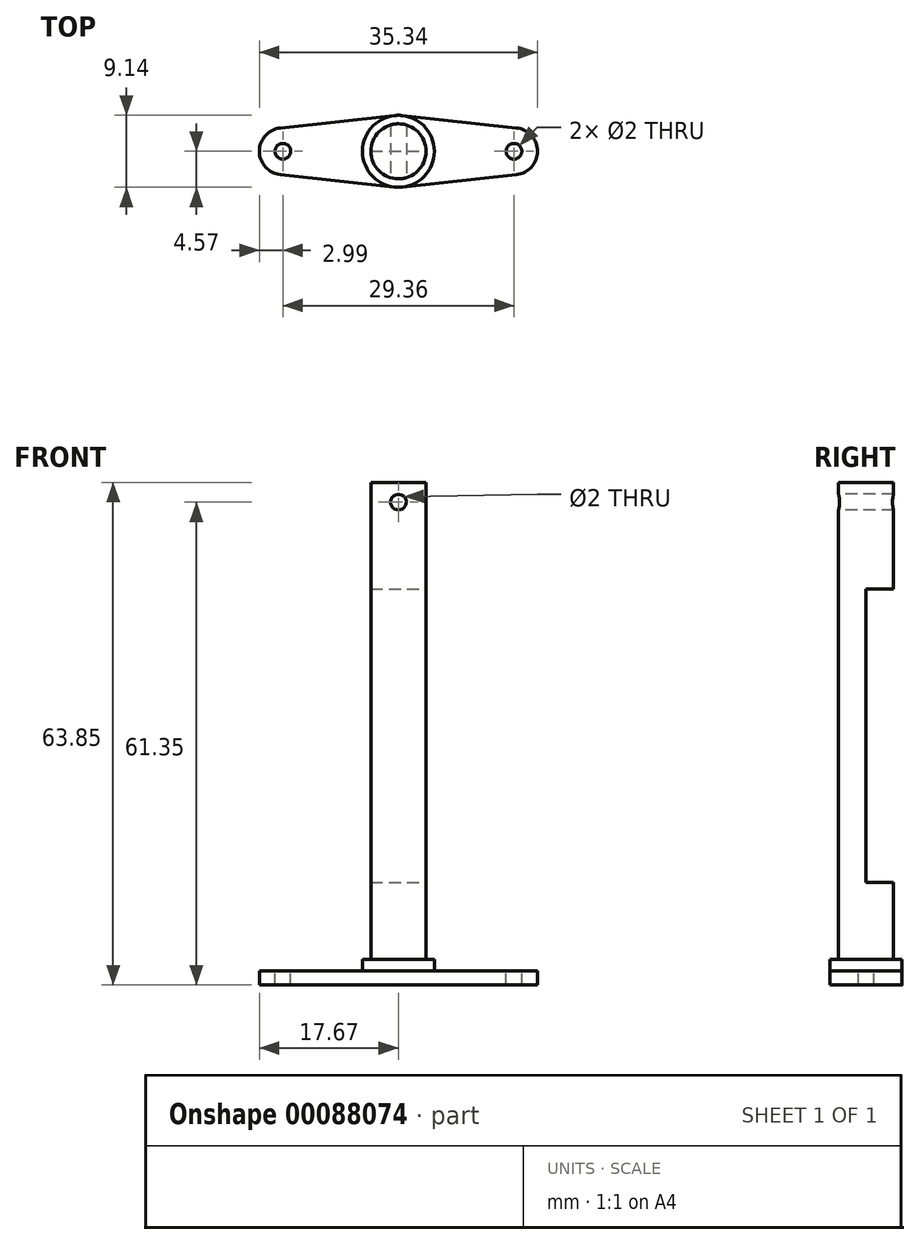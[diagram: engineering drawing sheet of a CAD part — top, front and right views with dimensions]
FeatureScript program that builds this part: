
annotation { "Feature Type Name" : "Feature", "Feature Type Description" : "" }
export const myFeature = defineFeature(function(context is Context, id is Id, definition is map)
    precondition{}
    {
        {
            var Q0;
            Q0=qCreatedBy(makeId("Top.planeOp"),FACE);
            var sketch = newSketch(context, id + "F0", { "sketchPlane" : qUnion([Q0])});
            skCircle(sketch, "E0", {"center": v(0, 0) * mm, "radius": 3.5 * mm});
            skSolve(sketch);
        }
        {
            var Q0;
            Q0 = qSketchRegion(id + "F0", true);
            extrude(context, id + "F1", {"entities" : qUnion([Q0]), "depth" : 56.35 * mm, "hasSecondDirection" : true, "secondDirectionOppositeDirection" : true, "secondDirectionDepth" : 1.5 * mm});
        }
        {
            var Q0;
            Q0=qCreatedBy(makeId("Top.planeOp"),FACE);
            var sketch = newSketch(context, id + "F2", { "sketchPlane" : qUnion([Q0])});
            skCircle(sketch, "E1", {"center": v(-14.68, 0) * mm, "radius": 1 * mm});
            skCircle(sketch, "E2.MirrorC", {"center": v(14.68, 0) * mm, "radius": 1 * mm});
            skArc(sketch, "E3", {"start": v(-15, 2.97) * mm, "mid": v(-16.9, 2) * mm, "end": v(-17.67, 0) * mm});
            skLineSegment(sketch, "E4", {"start": v(0, 0) * mm, "end": v(0, 4.6) * mm, "construction": true});
            skLineSegment(sketch, "E5", {"start": v(-15, 2.97) * mm, "end": v(0, 4.6) * mm});
            skLineSegment(sketch, "E6.MirrorCS", {"start": v(-15, -2.97) * mm, "end": v(0, -4.6) * mm});
            skArc(sketch, "E7.MirrorCS", {"start": v(-15, -2.97) * mm, "mid": v(-16.9, -2) * mm, "end": v(-17.67, 0) * mm});
            skLineSegment(sketch, "E8.MirrorCS", {"start": v(15, 2.97) * mm, "end": v(0, 4.6) * mm});
            skArc(sketch, "E9.MirrorCS", {"start": v(15, 2.97) * mm, "mid": v(16.9, 2) * mm, "end": v(17.67, 0) * mm});
            skArc(sketch, "E10.MirrorCS", {"start": v(15, -2.97) * mm, "mid": v(16.9, -2) * mm, "end": v(17.67, 0) * mm});
            skLineSegment(sketch, "E11.MirrorCS", {"start": v(15, -2.97) * mm, "end": v(0, -4.6) * mm});
            skSolve(sketch);
        }
        {
            var Q0;
            Q0 = qSketchRegion(id + "F2", true);
            extrude(context, id + "F3", {"entities" : qUnion([Q0]), "operationType" : NewBodyOperationType.ADD, "oppositeDirection" : true, "depth" : 2 * mm});
        }
        {
            var Q0;
            Q0=makeQuery(id+"F3.opExtrude","SWEPT_EDGE",EDGE,{"disambiguationData":[OSD([sQuery(id+"F2.wireOp",EDGE,"E5"),sQuery(id+"F2.wireOp",EDGE,"E8.MirrorCS")])]});
            fillet(context, id + "F4", {"entities" : qUnion([Q0]), "radius" : 5 * mm, "tangentPropagation" : true, "allowEdgeOverflow" : false});
        }
        {
            var Q0;
            Q0=makeQuery(id+"F3.opExtrude","SWEPT_EDGE",EDGE,{"disambiguationData":[OSD([sQuery(id+"F2.wireOp",EDGE,"E6.MirrorCS"),sQuery(id+"F2.wireOp",EDGE,"E11.MirrorCS")])]});
            fillet(context, id + "F5", {"entities" : qUnion([Q0]), "radius" : 5 * mm, "tangentPropagation" : true, "allowEdgeOverflow" : false});
        }
        {
            var Q0;
            Q0=qCreatedBy(makeId("Front.planeOp"),FACE);
            var sketch = newSketch(context, id + "F6", { "sketchPlane" : qUnion([Q0])});
            skLineSegment(sketch, "E12", {"start": v(4.63, 9.53) * mm, "end": v(4.63, 28.18) * mm});
            skLineSegment(sketch, "E13", {"start": v(4.63, 28.18) * mm, "end": v(-5.26, 28.18) * mm});
            skLineSegment(sketch, "E14", {"start": v(-5.26, 28.18) * mm, "end": v(-5.26, 9.53) * mm});
            skLineSegment(sketch, "E15", {"start": v(-19.44, 28.18) * mm, "end": v(29.53, 28.18) * mm, "construction": true});
            skLineSegment(sketch, "E16", {"start": v(-5.26, 9.53) * mm, "end": v(4.63, 9.53) * mm});
            skLineSegment(sketch, "E17.MirrorCS", {"start": v(-5.26, 28.18) * mm, "end": v(-5.26, 46.83) * mm});
            skLineSegment(sketch, "E18.MirrorCS", {"start": v(-5.26, 46.83) * mm, "end": v(4.63, 46.83) * mm});
            skLineSegment(sketch, "E19.MirrorCS", {"start": v(4.63, 46.83) * mm, "end": v(4.63, 28.18) * mm});
            skSolve(sketch);
        }
        {
            var Q0;
            Q0 = qSketchRegion(id + "F6", true);
            extrude(context, id + "F7", {"entities" : qUnion([Q0]), "operationType" : NewBodyOperationType.REMOVE, "oppositeDirection" : true, "depth" : 12.14 * mm});
        }
        {
            var Q0;
            Q0=makeQuery(id+"F1.opExtrude","CAP_FACE",FACE,{"disambiguationData":[OSD([sQuery(id+"F0.wireOp",EDGE,"E0")])],"isStart":false});
            extrude(context, id + "F8", {"entities" : qUnion([Q0]), "operationType" : NewBodyOperationType.ADD, "depth" : 4 * mm});
        }
        {
            var Q0;
            Q0=qCreatedBy(makeId("Front.planeOp"),FACE);
            var sketch = newSketch(context, id + "F9", { "sketchPlane" : qUnion([Q0])});
            skCircle(sketch, "E20", {"center": v(0, 57.85) * mm, "radius": 1 * mm});
            skSolve(sketch);
        }
        {
            var Q0;
            Q0 = qSketchRegion(id + "F9", true);
            extrude(context, id + "F10", {"entities" : qUnion([Q0]), "operationType" : NewBodyOperationType.REMOVE, "endBound" : BoundingType.SYMMETRIC, "oppositeDirection" : true, "depth" : 25 * mm});
        }
        {
            var Q0;
            Q0=makeQuery(id+"F3.opExtrude","CAP_FACE",FACE,{"disambiguationData":[OSD([sQuery(id+"F2.wireOp",EDGE,"E1"),sQuery(id+"F2.wireOp",EDGE,"E2.MirrorC"),sQuery(id+"F2.wireOp",EDGE,"E3"),sQuery(id+"F2.wireOp",EDGE,"E5"),sQuery(id+"F2.wireOp",EDGE,"E6.MirrorCS"),sQuery(id+"F2.wireOp",EDGE,"E7.MirrorCS"),sQuery(id+"F2.wireOp",EDGE,"E8.MirrorCS"),sQuery(id+"F2.wireOp",EDGE,"E9.MirrorCS"),sQuery(id+"F2.wireOp",EDGE,"E10.MirrorCS"),sQuery(id+"F2.wireOp",EDGE,"E11.MirrorCS")])],"isStart":false});
            var sketch = newSketch(context, id + "F11", { "sketchPlane" : qUnion([Q0])});
            skLineSegment(sketch, "E21", {"start": v(-15, 2.97) * mm, "end": v(-0.54, 4.54) * mm});
            skArc(sketch, "E22", {"start": v(-15, 2.97) * mm, "mid": v(-17.67, 0) * mm, "end": v(-15, -2.97) * mm});
            skLineSegment(sketch, "E23", {"start": v(-15, -2.97) * mm, "end": v(-0.54, -4.54) * mm});
            skArc(sketch, "E24", {"start": v(0.54, 4.54) * mm, "mid": v(0, 4.57) * mm, "end": v(-0.54, 4.54) * mm});
            skArc(sketch, "E25.MirrorCS", {"start": v(0.54, -4.54) * mm, "mid": v(0, -4.57) * mm, "end": v(-0.54, -4.54) * mm});
            skLineSegment(sketch, "E26.MirrorCS", {"start": v(15, 2.97) * mm, "end": v(0.54, 4.54) * mm});
            skArc(sketch, "E27.MirrorCS", {"start": v(15, 2.97) * mm, "mid": v(17.67, 0) * mm, "end": v(15, -2.97) * mm});
            skLineSegment(sketch, "E28.MirrorCS", {"start": v(15, -2.97) * mm, "end": v(0.54, -4.54) * mm});
            skCircle(sketch, "E29", {"center": v(-14.68, 0) * mm, "radius": 1 * mm});
            skCircle(sketch, "E30.MirrorC", {"center": v(14.68, 0) * mm, "radius": 1 * mm});
            skSolve(sketch);
        }
        {
            var Q0;
            Q0 = qSketchRegion(id + "F11", true);
            extrude(context, id + "F12", {"entities" : qUnion([Q0]), "operationType" : NewBodyOperationType.ADD, "depth" : 1.5 * mm});
        }
        {
            var Q0;
            Q0=makeQuery(id+"F3.opExtrude","CAP_FACE",FACE,{"disambiguationData":[OSD([sQuery(id+"F2.wireOp",EDGE,"E1"),sQuery(id+"F2.wireOp",EDGE,"E2.MirrorC"),sQuery(id+"F2.wireOp",EDGE,"E3"),sQuery(id+"F2.wireOp",EDGE,"E5"),sQuery(id+"F2.wireOp",EDGE,"E6.MirrorCS"),sQuery(id+"F2.wireOp",EDGE,"E7.MirrorCS"),sQuery(id+"F2.wireOp",EDGE,"E8.MirrorCS"),sQuery(id+"F2.wireOp",EDGE,"E9.MirrorCS"),sQuery(id+"F2.wireOp",EDGE,"E10.MirrorCS"),sQuery(id+"F2.wireOp",EDGE,"E11.MirrorCS")])],"isStart":true});
            var sketch = newSketch(context, id + "F13", { "sketchPlane" : qUnion([Q0])});
            skLineSegment(sketch, "E31", {"start": v(15, -2.97) * mm, "end": v(0.54, -4.54) * mm});
            skLineSegment(sketch, "E32", {"start": v(15, 2.97) * mm, "end": v(0.54, 4.54) * mm});
            skArc(sketch, "E33", {"start": v(15, -2.97) * mm, "mid": v(17.67, 0) * mm, "end": v(15, 2.97) * mm});
            skCircle(sketch, "E34", {"center": v(14.68, 0) * mm, "radius": 1 * mm});
            skLineSegment(sketch, "E35.MirrorCS", {"start": v(-15, 2.97) * mm, "end": v(-0.54, 4.54) * mm});
            skArc(sketch, "E36.MirrorCS", {"start": v(-15, -2.97) * mm, "mid": v(-17.67, 0) * mm, "end": v(-15, 2.97) * mm});
            skLineSegment(sketch, "E37.MirrorCS", {"start": v(-15, -2.97) * mm, "end": v(-0.54, -4.54) * mm});
            skArc(sketch, "E38", {"start": v(0.54, 4.54) * mm, "mid": v(0, 4.57) * mm, "end": v(-0.54, 4.54) * mm});
            skArc(sketch, "E39", {"start": v(-0.54, -4.54) * mm, "mid": v(0, -4.57) * mm, "end": v(0.54, -4.54) * mm});
            skCircle(sketch, "E40", {"center": v(0, 0) * mm, "radius": 3.5 * mm});
            skCircle(sketch, "E41.MirrorC", {"center": v(-14.68, 0) * mm, "radius": 1 * mm});
            skSolve(sketch);
        }
        {
            var Q0;
            Q0 = qSketchRegion(id + "F13", true);
            extrude(context, id + "F14", {"entities" : qUnion([Q0]), "operationType" : NewBodyOperationType.REMOVE, "oppositeDirection" : true, "depth" : 1.71 * mm});
        }
        {
            var Q0;
            Q0=makeQuery(id+"F14.boolean.opBoolean","COPY",FACE,{"derivedFrom":makeQuery(id+"F14.opExtrude","CAP_FACE",FACE,{"disambiguationData":[OSD([sQuery(id+"F13.wireOp",EDGE,"E31"),sQuery(id+"F13.wireOp",EDGE,"E32"),sQuery(id+"F13.wireOp",EDGE,"E33"),sQuery(id+"F13.wireOp",EDGE,"E34"),sQuery(id+"F13.wireOp",EDGE,"E35.MirrorCS"),sQuery(id+"F13.wireOp",EDGE,"E36.MirrorCS"),sQuery(id+"F13.wireOp",EDGE,"E37.MirrorCS"),sQuery(id+"F13.wireOp",EDGE,"E38"),sQuery(id+"F13.wireOp",EDGE,"E39"),sQuery(id+"F13.wireOp",EDGE,"E40"),sQuery(id+"F13.wireOp",EDGE,"E41.MirrorC")])],"isStart":false})});
            var sketch = newSketch(context, id + "F15", { "sketchPlane" : qUnion([Q0])});
            skCircle(sketch, "E42", {"center": v(0, 0) * mm, "radius": 4.57 * mm});
            skSolve(sketch);
        }
        {
            var Q0;
            Q0 = qSketchRegion(id + "F15", true);
            extrude(context, id + "F16", {"entities" : qUnion([Q0]), "operationType" : NewBodyOperationType.ADD, "depth" : 1.5 * mm});
        }
    });
